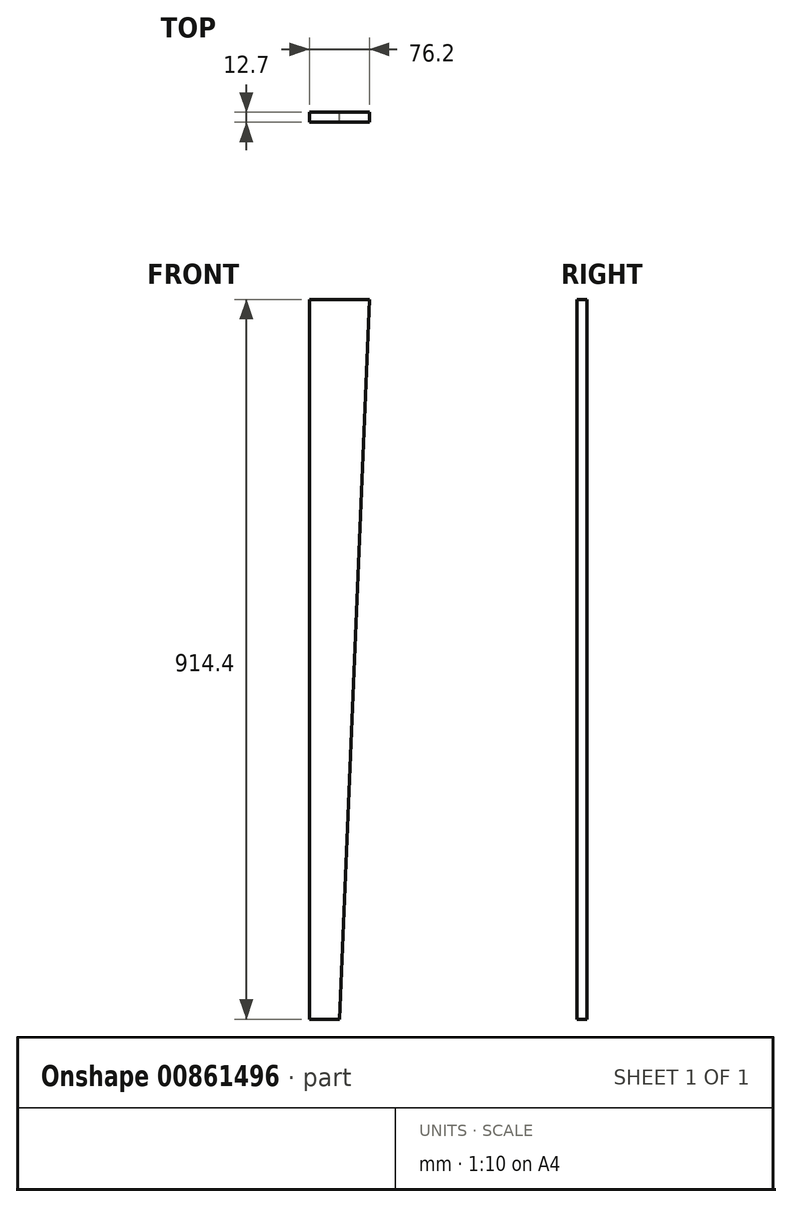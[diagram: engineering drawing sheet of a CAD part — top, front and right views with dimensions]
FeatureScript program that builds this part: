
annotation { "Feature Type Name" : "Feature", "Feature Type Description" : "" }
export const myFeature = defineFeature(function(context is Context, id is Id, definition is map)
    precondition{}
    {
        {
            var Q0;
            Q0=qCreatedBy(makeId("Front.planeOp"),FACE);
            var sketch = newSketch(context, id + "F0", { "sketchPlane" : qUnion([Q0])});
            skLineSegment(sketch, "E0", {"start": v(0, 0) * mm, "end": v(0, -914.4) * mm});
            skLineSegment(sketch, "E1", {"start": v(0, -914.4) * mm, "end": v(38.1, -914.4) * mm});
            skLineSegment(sketch, "E2", {"start": v(38.1, -914.4) * mm, "end": v(76.2, 0) * mm});
            skLineSegment(sketch, "E3", {"start": v(76.2, 0) * mm, "end": v(0, 0) * mm});
            skSolve(sketch);
        }
        {
            var Q0;
            Q0=makeQuery(id+"F0.imprint","IMPRINT",FACE,{"disambiguationData":[TD([[makeQuery(id+"F0.imprint","IMPRINT",EDGE,{"derivedFrom":sQuery(id+"F0.wireOp",EDGE,"E0")}),1.0]])]});
            extrude(context, id + "F1", {"entities" : qUnion([Q0]), "depth" : 12.7 * mm, "offsetDistance" : 25.4 * mm});
        }
    });
